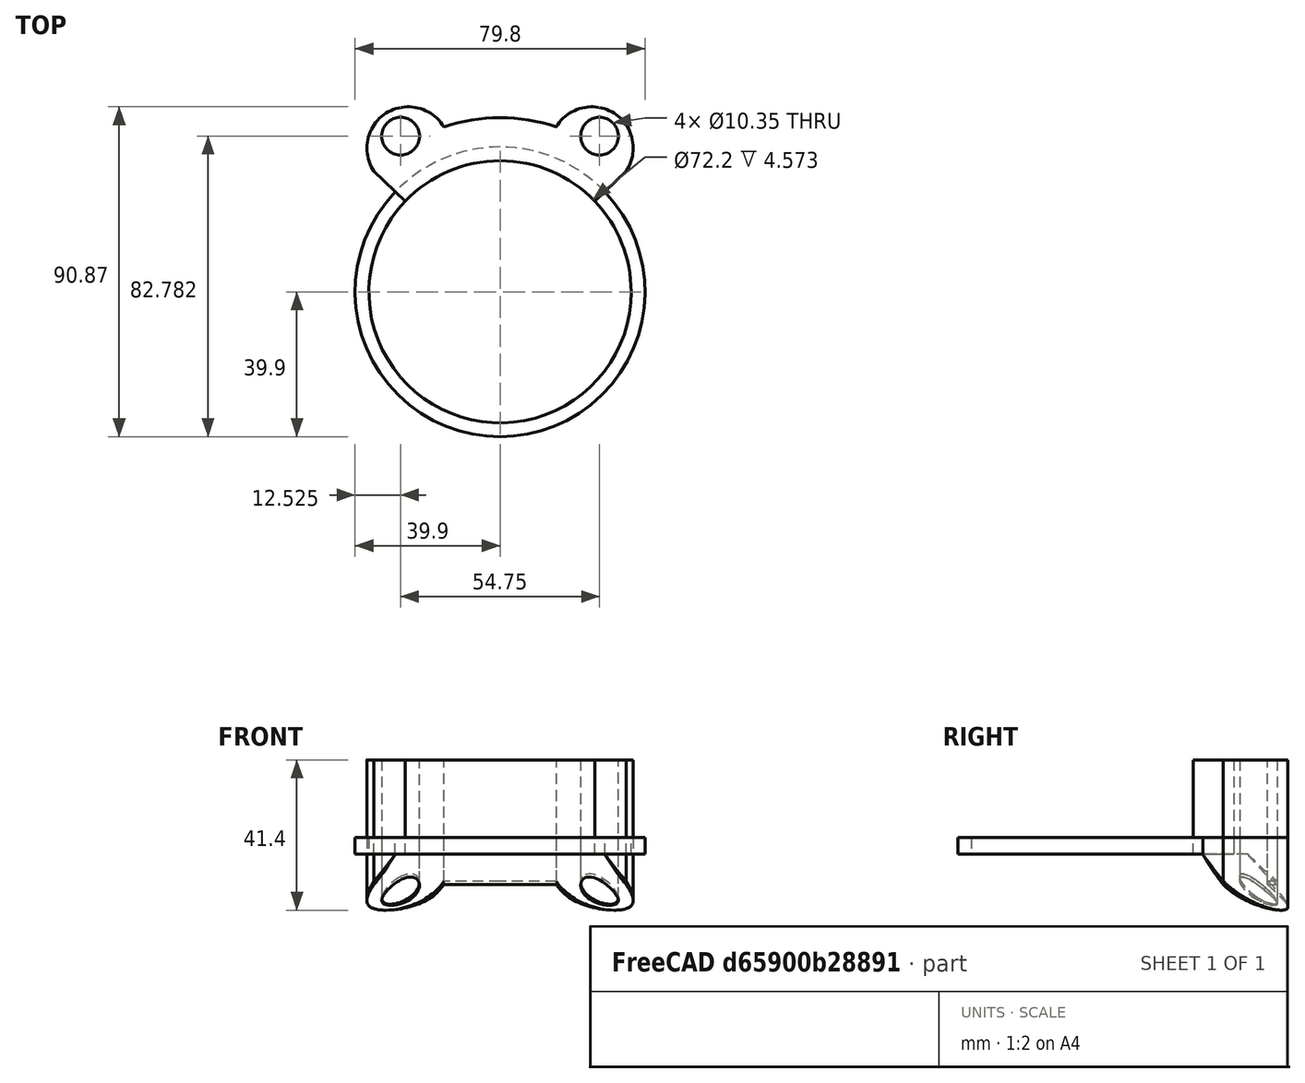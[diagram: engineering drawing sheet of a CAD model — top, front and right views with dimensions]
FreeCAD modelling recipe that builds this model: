
FCSTD DOCUMENT  (FreeCAD 0.17R13541 (Git))
Label: spacer
License: All rights reserved
LicenseURL: http://en.wikipedia.org/wiki/All_rights_reserved
objects: Mesh::Feature×11, Sketcher::SketchObject×4, PartDesign::Body×4, PartDesign::Pad×2, PartDesign::Revolution×2, Part::Cut×2, App::Part×2, App::DocumentObjectGroup×1
note: 18 computed .brp shape members not serialized (recipe doc carries the construction recipe); baked Part::Feature solids carry a one-line shape summary decoded from their .brp

FEATURE [Sketcher::SketchObject] Sketch  label="outer_sketch_right"
  MapMode = 5
  Support = -> [XY_Plane001]
  expr: Constraints.face_radius = 79.800000000000011mm / 2
  expr: Constraints[12] = 10.35mm / 2
  expr: Constraints.enclosure_radius = 96mm / 2
  expr: Constraints[27] = 22.800000000000001mm / 2
  expr: Constraints.outer_opening_outer_radius = 72.200000000000003mm / 2
  expr: Constraints.outer_opening_inner_radius = 62.799999999999997mm / 2
  sketch-geometry (34):
    g0: Circle [constr] CenterX=0 CenterY=0 CenterZ=0 NormalX=0 NormalY=0 NormalZ=1 AngleXU=0 Radius=48
    g1: Circle CenterX=-27.375 CenterY=42.8821 CenterZ=0 NormalX=0 NormalY=0 NormalZ=1 AngleXU=0 Radius=5.175
    g2: Circle [constr] CenterX=0 CenterY=0 CenterZ=0 NormalX=0 NormalY=0 NormalZ=1 AngleXU=0 Radius=36.1
    g3: Circle [constr] CenterX=0 CenterY=0 CenterZ=0 NormalX=0 NormalY=0 NormalZ=1 AngleXU=0 Radius=31.4
    g4: LineSegment [constr] StartX=0 StartY=0 StartZ=0 EndX=-31.3972 EndY=49.1827 EndZ=0
    g5: GeomPoint X=-16.8958 Y=26.4668 Z=0
    g6: GeomPoint X=-24.5904 Y=38.5201 Z=0
    g7: Circle CenterX=27.375 CenterY=42.8821 CenterZ=0 NormalX=0 NormalY=0 NormalZ=1 AngleXU=0 Radius=5.175
    g8: LineSegment [constr] StartX=0 StartY=0 StartZ=0 EndX=31.3972 EndY=49.1827 EndZ=0
    g9: GeomPoint X=16.8958 Y=26.4668 Z=0
    g10: GeomPoint X=24.5904 Y=38.5201 Z=0
    g11: LineSegment [constr] StartX=-32.55 StartY=42.8821 StartZ=0 EndX=32.55 EndY=42.8821 EndZ=0
    g12: GeomPoint X=-22.2 Y=42.8821 Z=0
    g13: GeomPoint X=22.2 Y=42.8821 Z=0
    g14: Circle [constr] CenterX=-25.263 CenterY=39.5738 CenterZ=0 NormalX=0 NormalY=0 NormalZ=1 AngleXU=0 Radius=11.4
    g15: Circle [constr] CenterX=25.263 CenterY=39.5738 CenterZ=0 NormalX=0 NormalY=0 NormalZ=1 AngleXU=0 Radius=11.4
    g16: GeomPoint X=-30.1596 Y=47.2441 Z=0
    g17: GeomPoint X=30.1596 Y=47.2441 Z=0
    g18: GeomPoint X=-34.6947 Y=33.1704 Z=0
    g19: GeomPoint X=-15.4845 Y=45.4338 Z=0
    g20: GeomPoint X=34.6947 Y=33.1704 Z=0
    g21: GeomPoint X=15.4845 Y=45.4338 Z=0
    g22: ArcOfCircle CenterX=-25.263 CenterY=39.5738 CenterZ=0 NormalX=0 NormalY=0 NormalZ=1 AngleXU=0 Radius=11.4 StartAngle=0.539887 EndAngle=3.73803
    g23: ArcOfCircle CenterX=0 CenterY=0 CenterZ=0 NormalX=0 NormalY=0 NormalZ=1 AngleXU=0 Radius=48 StartAngle=1.24233 EndAngle=1.89926
    g24: ArcOfCircle CenterX=25.263 CenterY=39.5738 CenterZ=0 NormalX=0 NormalY=0 NormalZ=1 AngleXU=0 Radius=11.4 StartAngle=5.68675 EndAngle=8.88489
    g25: LineSegment [constr] StartX=0 StartY=0 StartZ=0 EndX=-34.6947 EndY=33.1704 EndZ=0
    g26: LineSegment [constr] StartX=0 StartY=0 StartZ=0 EndX=34.6947 EndY=33.1704 EndZ=0
    g27: LineSegment StartX=-28.84 StartY=27.5729 StartZ=0 EndX=-34.6947 EndY=33.1704 EndZ=0
    g28: LineSegment StartX=28.84 StartY=27.5729 StartZ=0 EndX=34.6947 EndY=33.1704 EndZ=0
    g29: Circle [constr] CenterX=0 CenterY=0 CenterZ=0 NormalX=0 NormalY=0 NormalZ=1 AngleXU=0 Radius=39.9
    g30: GeomPoint X=-27.375 Y=42.8821 Z=0
    g31: GeomPoint X=27.375 Y=42.8821 Z=0
    g32: ArcOfCircle CenterX=0 CenterY=0 CenterZ=0 NormalX=0 NormalY=0 NormalZ=1 AngleXU=0 Radius=39.9 StartAngle=2.37865 EndAngle=7.04613
    g33: Circle CenterX=0 CenterY=0 CenterZ=0 NormalX=0 NormalY=0 NormalZ=1 AngleXU=0 Radius=36.1
  constraints (84):
    c: Coincident(g0,g-1)
    c: Radius(g0) = 48  'enclosure_radius'
    c: Coincident(g2,g-1)
    c: Radius(g2) = 36.1  'outer_opening_outer_radius'
    c: Coincident(g3,g-1)
    c: Radius(g3) = 31.4  'outer_opening_inner_radius'
    c: Coincident(g4,g-1)
    c: PointOnObject(g5,g4)
    c: PointOnObject(g5,g3)
    c: PointOnObject(g6,g4)
    c: PointOnObject(g6,g1)
    c: Distance(g5,g6) = 14.3
    c: Radius(g1) = 5.175
    c: Coincident(g8,g-1)
    c: PointOnObject(g9,g8)
    c: PointOnObject(g10,g8)
    c: PointOnObject(g9,g3)
    c: PointOnObject(g10,g7)
    c: Equal(g1,g7)
    c: Distance(g9,g10) = 14.3
    c: Horizontal(g11)
    c: PointOnObject(g12,g11)
    c: PointOnObject(g13,g11)
    c: PointOnObject(g12,g1)
    c: PointOnObject(g13,g7)
    c: PointOnObject(g14,g4)
    c: PointOnObject(g15,g8)
    c: Radius(g15) = 11.4
    c: Equal(g15,g14)
    c: PointOnObject(g1,g4)
    c: PointOnObject(g4,g14)
    c: PointOnObject(g7,g8)
    c: PointOnObject(g8,g15)
    c: PointOnObject(g16,g4)
    c: PointOnObject(g17,g8)
    c: PointOnObject(g16,g1)
    c: PointOnObject(g17,g7)
    c: Distance(g17,g8) = 2.3
    c: Distance(g16,g4) = 2.3
    c: PointOnObject(g18,g0)
    c: PointOnObject(g19,g0)
    c: PointOnObject(g20,g0)
    c: PointOnObject(g21,g0)
    c: PointOnObject(g18,g14)
    c: PointOnObject(g19,g14)
    c: PointOnObject(g21,g15)
    c: PointOnObject(g20,g15)
    c: Coincident(g22,g14)
    c: Coincident(g22,g18)
    c: PointOnObject(g22,g0)
    c: Coincident(g23,g-1)
    c: Coincident(g23,g19)
    c: PointOnObject(g23,g15)
    c: Coincident(g24,g15)
    c: Coincident(g24,g21)
    c: PointOnObject(g24,g0)
    c: Coincident(g25,g-1)
    c: Coincident(g25,g18)
    c: Coincident(g26,g-1)
    c: Coincident(g26,g20)
    c: Coincident(g27,g18)
    c: Coincident(g28,g20)
    c: Coincident(g29,g-1)
    c: Radius(g29) = 39.9  'face_radius'
    c: Distance(g-1,g4) = 58.35  'outer_radius'
    c: Distance(g5,g4) = 26.95
    c: Distance(g9,g8) = 26.95
    c: PointOnObject(g30,g11)
    c: PointOnObject(g31,g11)
    c: Coincident(g30,g1)
    c: Coincident(g31,g7)
    c: PointOnObject(g11,g1)
    c: PointOnObject(g11,g7)
    c: Distance(g11,g11) = 65.1
    c: Distance(g1,g7) = 54.75
    c: PointOnObject(g28,g29)
    c: PointOnObject(g28,g26)
    c: PointOnObject(g27,g29)
    c: PointOnObject(g27,g25)
    c: Coincident(g32,g-1)
    c: Coincident(g32,g27)
    c: PointOnObject(g32,g26)
    c: Coincident(g33,g-1)
    c: Equal(g33,g2)
FEATURE [Sketcher::SketchObject] Sketch002  label="chamfer_sketch_right"
  MapMode = 5
  Placement = pos=(0,0,0) rot=(0.57735,0.57735,0.57735;2.0944rad)
  Support = -> [YZ_Plane002]
  expr: Constraints[9] = outer_sketch.Constraints.outer_opening_outer_radius
  expr: Constraints[8] = Sketch.Constraints.outer_radius
  expr: Constraints[10] = Sketch.Constraints.face_radius
  sketch-geometry (7):
    g0: LineSegment StartX=36.1 StartY=15.4272 StartZ=0 EndX=39.9 EndY=15.4272 EndZ=0
    g1: LineSegment [constr] StartX=39.9 StartY=15.4272 StartZ=0 EndX=58.35 EndY=1.2e-11 EndZ=0
    g2: LineSegment StartX=58.35 StartY=1.2e-11 StartZ=0 EndX=58.35 EndY=-5 EndZ=0
    g3: LineSegment StartX=58.35 StartY=-5 StartZ=0 EndX=36.1 EndY=-5 EndZ=0
    g4: LineSegment StartX=36.1 StartY=-5 StartZ=0 EndX=36.1 EndY=15.4272 EndZ=0
    g5: LineSegment [constr] StartX=49.125 StartY=7.71362 StartZ=0 EndX=48.8043 EndY=7.33005 EndZ=0
    g6: ArcOfCircle CenterX=141.721 CenterY=118.452 CenterZ=0 NormalX=0 NormalY=0 NormalZ=1 AngleXU=0 Radius=144.851 StartAngle=3.93287 EndAngle=4.09909
  constraints (22):
    c: Horizontal(g0)
    c: Coincident(g0,g1)
    c: Vertical(g2)
    c: Coincident(g2,g3)
    c: Horizontal(g3)
    c: Coincident(g3,g4)
    c: Coincident(g4,g0)
    c: Vertical(g4)
    c: DistanceX(g-1,g1) = 58.35
    c: DistanceX(g-1,g0) = 36.1
    c: DistanceX(g-1,g0) = 39.9
    c: Coincident(g1,g2)
    c: PointOnObject(g1,g-1)
    c: Distance(g2) = 5
    c: Distance(g1) = 24.05
    c: PointOnObject(g5,g1)
    c: Perpendicular(g1,g5)
    c: Symmetric(g0,g1,g5)
    c: Distance(g5) = 0.5  'chamfer_deflection'
    c: Coincident(g6,g0)
    c: Coincident(g6,g1)
    c: PointOnObject(g5,g6)
FEATURE [PartDesign::Pad] Pad
  Length = 20
  Length2 = 100
  Profile = -> Sketch
  Type = 0
FEATURE [PartDesign::Body] Body  label="case_right"
  Group = -> [Sketch,Pad]
  Origin = -> Origin001
  Tip = -> Pad
FEATURE [PartDesign::Revolution] Revolution
  Angle = 360
  Axis = (0,0,1)
  Base = (0,0,0)
  Placement = pos=(0,0,0) rot=(0.57735,0.57735,0.57735;2.0944rad)
  Profile = -> Sketch002
  ReferenceAxis = -> Sketch002 [V_Axis]
  Reversed = true
FEATURE [PartDesign::Body] Body001  label="chamfer_cutout_right"
  Group = -> [Sketch002,Revolution]
  Origin = -> Origin002
  Tip = -> Revolution
FEATURE [Mesh::Feature] Mesh  label="spacer_mesh"
FEATURE [Mesh::Feature] Mesh001  label="spacer_mesh2-0"
FEATURE [Mesh::Feature] Mesh002  label="spacer_mesh2-1.2"
FEATURE [Mesh::Feature] Mesh003  label="spacer_mesh3-1.2"
FEATURE [Mesh::Feature] Mesh004  label="spacer_mesh3-0.5"
FEATURE [Mesh::Feature] Mesh005  label="spacer_mesh4-0.5"
FEATURE [Mesh::Feature] Mesh006  label="spacer_mesh4-1.2"
FEATURE [Mesh::Feature] Mesh007  label="spacer_mesh5-1.2"
FEATURE [Mesh::Feature] Mesh008  label="spacer_mesh5-0.5"
FEATURE [Sketcher::SketchObject] Sketch004  label="outer_sketch001"
  MapMode = 5
  Support = -> [XY_Plane005]
  expr: Constraints.outer_opening_inner_radius = 62.799999999999997mm / 2
  expr: Constraints.outer_opening_outer_radius = 72.200000000000003mm / 2
  expr: Constraints[27] = 22.800000000000001mm / 2
  expr: Constraints.enclosure_radius = 96mm / 2
  expr: Constraints.face_radius = 79.800000000000011mm / 2
  expr: Constraints[12] = 10.35mm / 2
  sketch-geometry (33):
    g0: Circle [constr] CenterX=0 CenterY=0 CenterZ=0 NormalX=0 NormalY=0 NormalZ=1 AngleXU=0 Radius=48
    g1: Circle CenterX=-27.375 CenterY=42.8821 CenterZ=0 NormalX=0 NormalY=0 NormalZ=1 AngleXU=0 Radius=5.175
    g2: Circle [constr] CenterX=0 CenterY=0 CenterZ=0 NormalX=0 NormalY=0 NormalZ=1 AngleXU=0 Radius=36.1
    g3: Circle [constr] CenterX=0 CenterY=0 CenterZ=0 NormalX=0 NormalY=0 NormalZ=1 AngleXU=0 Radius=31.4
    g4: LineSegment [constr] StartX=0 StartY=0 StartZ=0 EndX=-31.3972 EndY=49.1827 EndZ=0
    g5: GeomPoint X=-16.8958 Y=26.4668 Z=0
    g6: GeomPoint X=-24.5904 Y=38.5201 Z=0
    g7: Circle CenterX=27.375 CenterY=42.8821 CenterZ=0 NormalX=0 NormalY=0 NormalZ=1 AngleXU=0 Radius=5.175
    g8: LineSegment [constr] StartX=0 StartY=0 StartZ=0 EndX=31.3972 EndY=49.1827 EndZ=0
    g9: GeomPoint X=16.8958 Y=26.4668 Z=0
    g10: GeomPoint X=24.5904 Y=38.5201 Z=0
    g11: LineSegment [constr] StartX=-32.55 StartY=42.8821 StartZ=0 EndX=32.55 EndY=42.8821 EndZ=0
    g12: GeomPoint X=-22.2 Y=42.8821 Z=0
    g13: GeomPoint X=22.2 Y=42.8821 Z=0
    g14: Circle [constr] CenterX=-25.263 CenterY=39.5738 CenterZ=0 NormalX=0 NormalY=0 NormalZ=1 AngleXU=0 Radius=11.4
    g15: Circle [constr] CenterX=25.263 CenterY=39.5738 CenterZ=0 NormalX=0 NormalY=0 NormalZ=1 AngleXU=0 Radius=11.4
    g16: GeomPoint X=-30.1596 Y=47.2441 Z=0
    g17: GeomPoint X=30.1596 Y=47.2441 Z=0
    g18: GeomPoint X=-34.6947 Y=33.1704 Z=0
    g19: GeomPoint X=-15.4845 Y=45.4338 Z=0
    g20: GeomPoint X=34.6947 Y=33.1704 Z=0
    g21: GeomPoint X=15.4845 Y=45.4338 Z=0
    g22: ArcOfCircle CenterX=-25.263 CenterY=39.5738 CenterZ=0 NormalX=0 NormalY=0 NormalZ=1 AngleXU=0 Radius=11.4 StartAngle=0.539887 EndAngle=3.73803
    g23: ArcOfCircle CenterX=0 CenterY=0 CenterZ=0 NormalX=0 NormalY=0 NormalZ=1 AngleXU=0 Radius=48 StartAngle=1.24233 EndAngle=1.89926
    g24: ArcOfCircle CenterX=25.263 CenterY=39.5738 CenterZ=0 NormalX=0 NormalY=0 NormalZ=1 AngleXU=0 Radius=11.4 StartAngle=5.68675 EndAngle=8.88489
    g25: LineSegment [constr] StartX=0 StartY=0 StartZ=0 EndX=-34.6947 EndY=33.1704 EndZ=0
    g26: LineSegment [constr] StartX=0 StartY=0 StartZ=0 EndX=34.6947 EndY=33.1704 EndZ=0
    g27: ArcOfCircle CenterX=0 CenterY=0 CenterZ=0 NormalX=0 NormalY=0 NormalZ=1 AngleXU=0 Radius=36.1 StartAngle=0.762941 EndAngle=2.37865
    g28: LineSegment StartX=-26.0933 StartY=24.9469 StartZ=0 EndX=-34.6947 EndY=33.1704 EndZ=0
    g29: LineSegment StartX=26.0933 StartY=24.9469 StartZ=0 EndX=34.6947 EndY=33.1704 EndZ=0
    g30: Circle [constr] CenterX=0 CenterY=0 CenterZ=0 NormalX=0 NormalY=0 NormalZ=1 AngleXU=0 Radius=39.9
    g31: GeomPoint X=-27.375 Y=42.8821 Z=0
    g32: GeomPoint X=27.375 Y=42.8821 Z=0
  constraints (81):
    c: Coincident(g0,g-1)
    c: Radius(g0) = 48  'enclosure_radius'
    c: Coincident(g2,g-1)
    c: Radius(g2) = 36.1  'outer_opening_outer_radius'
    c: Coincident(g3,g-1)
    c: Radius(g3) = 31.4  'outer_opening_inner_radius'
    c: Coincident(g4,g-1)
    c: PointOnObject(g5,g4)
    c: PointOnObject(g5,g3)
    c: PointOnObject(g6,g4)
    c: PointOnObject(g6,g1)
    c: Distance(g5,g6) = 14.3
    c: Radius(g1) = 5.175
    c: Coincident(g8,g-1)
    c: PointOnObject(g9,g8)
    c: PointOnObject(g10,g8)
    c: PointOnObject(g9,g3)
    c: PointOnObject(g10,g7)
    c: Equal(g1,g7)
    c: Distance(g9,g10) = 14.3
    c: Horizontal(g11)
    c: PointOnObject(g12,g11)
    c: PointOnObject(g13,g11)
    c: PointOnObject(g12,g1)
    c: PointOnObject(g13,g7)
    c: PointOnObject(g14,g4)
    c: PointOnObject(g15,g8)
    c: Radius(g15) = 11.4
    c: Equal(g15,g14)
    c: PointOnObject(g1,g4)
    c: PointOnObject(g4,g14)
    c: PointOnObject(g7,g8)
    c: PointOnObject(g8,g15)
    c: PointOnObject(g16,g4)
    c: PointOnObject(g17,g8)
    c: PointOnObject(g16,g1)
    c: PointOnObject(g17,g7)
    c: Distance(g17,g8) = 2.3
    c: Distance(g16,g4) = 2.3
    c: PointOnObject(g18,g0)
    c: PointOnObject(g19,g0)
    c: PointOnObject(g20,g0)
    c: PointOnObject(g21,g0)
    c: PointOnObject(g18,g14)
    c: PointOnObject(g19,g14)
    c: PointOnObject(g21,g15)
    c: PointOnObject(g20,g15)
    c: Coincident(g22,g14)
    c: Coincident(g22,g18)
    c: PointOnObject(g22,g0)
    c: Coincident(g23,g-1)
    c: Coincident(g23,g19)
    c: PointOnObject(g23,g15)
    c: Coincident(g24,g15)
    c: Coincident(g24,g21)
    c: PointOnObject(g24,g0)
    c: Coincident(g25,g-1)
    c: Coincident(g25,g18)
    c: Coincident(g26,g-1)
    c: Coincident(g26,g20)
    c: Coincident(g27,g-1)
    c: PointOnObject(g27,g2)
    c: PointOnObject(g27,g26)
    c: PointOnObject(g27,g25)
    c: Coincident(g28,g27)
    c: Coincident(g28,g18)
    c: Coincident(g29,g27)
    c: Coincident(g29,g20)
    c: Coincident(g30,g-1)
    c: Radius(g30) = 39.9  'face_radius'
    c: Distance(g-1,g4) = 58.35  'outer_radius'
    c: Distance(g5,g4) = 26.95
    c: Distance(g9,g8) = 26.95
    c: PointOnObject(g31,g11)
    c: PointOnObject(g32,g11)
    c: Coincident(g31,g1)
    c: Coincident(g32,g7)
    c: PointOnObject(g11,g1)
    c: PointOnObject(g11,g7)
    c: Distance(g11,g11) = 65.1
    c: Distance(g1,g7) = 54.75
FEATURE [Sketcher::SketchObject] Sketch005  label="chamfer_sketch_left"
  MapMode = 5
  Placement = pos=(0,0,0) rot=(0.57735,0.57735,0.57735;2.0944rad)
  Support = -> [YZ_Plane006]
  expr: Constraints[9] = outer_sketch.Constraints.outer_opening_outer_radius
  expr: Constraints[8] = Sketch.Constraints.outer_radius
  expr: Constraints[10] = Sketch.Constraints.face_radius
  sketch-geometry (7):
    g0: LineSegment StartX=36.1 StartY=15.4272 StartZ=0 EndX=39.9 EndY=15.4272 EndZ=0
    g1: LineSegment [constr] StartX=39.9 StartY=15.4272 StartZ=0 EndX=58.35 EndY=0 EndZ=0
    g2: LineSegment StartX=58.35 StartY=0 StartZ=0 EndX=58.35 EndY=-5 EndZ=0
    g3: LineSegment StartX=58.35 StartY=-5 StartZ=0 EndX=36.1 EndY=-5 EndZ=0
    g4: LineSegment StartX=36.1 StartY=-5 StartZ=0 EndX=36.1 EndY=15.4272 EndZ=0
    g5: LineSegment [constr] StartX=49.125 StartY=7.71362 StartZ=0 EndX=48.3552 EndY=6.79304 EndZ=0
    g6: ArcOfCircle CenterX=87.3886 CenterY=53.4744 CenterZ=0 NormalX=0 NormalY=0 NormalZ=1 AngleXU=0 Radius=60.8503 StartAngle=3.81706 EndAngle=4.21491
  constraints (22):
    c: Horizontal(g0)
    c: Coincident(g0,g1)
    c: Vertical(g2)
    c: Coincident(g2,g3)
    c: Horizontal(g3)
    c: Coincident(g3,g4)
    c: Coincident(g4,g0)
    c: Vertical(g4)
    c: DistanceX(g-1,g1) = 58.35
    c: DistanceX(g-1,g0) = 36.1
    c: DistanceX(g-1,g0) = 39.9
    c: Coincident(g1,g2)
    c: PointOnObject(g1,g-1)
    c: Distance(g2) = 5
    c: Distance(g1) = 24.05
    c: PointOnObject(g5,g1)
    c: Perpendicular(g1,g5)
    c: Symmetric(g0,g1,g5)
    c: Distance(g5) = 1.2  'chamfer_deflection'
    c: Coincident(g6,g0)
    c: Coincident(g6,g1)
    c: PointOnObject(g5,g6)
FEATURE [PartDesign::Pad] Pad002
  Length = 41.4
  Length2 = 100
  Profile = -> Sketch004
  Type = 0
FEATURE [PartDesign::Body] Body005  label="case_left"
  Group = -> [Sketch004,Pad002]
  Origin = -> Origin006
  Tip = -> Pad002
FEATURE [PartDesign::Revolution] Revolution001
  Angle = 360
  Axis = (0,0,1)
  Base = (0,0,0)
  Placement = pos=(0,0,0) rot=(0.57735,0.57735,0.57735;2.0944rad)
  Profile = -> Sketch005
  ReferenceAxis = -> Sketch005 [V_Axis]
  Reversed = true
FEATURE [PartDesign::Body] Body004  label="chamfer_cutout_left"
  Group = -> [Sketch005,Revolution001]
  Origin = -> Origin007
  Tip = -> Revolution001
FEATURE [Part::Cut] Cut  label="spacer_right"
  Base = -> Body
  Tool = -> Body001
FEATURE [App::Part] Part  label="spacer_right_part"
  Group = -> [Body,Body001,Cut]
  License = CC BY 3.0
  LicenseURL = http://creativecommons.org/licenses/by/3.0/
  Origin = -> Origin
FEATURE [Part::Cut] Cut001  label="spacer_left"
  Base = -> Body005
  Tool = -> Body004
FEATURE [App::Part] Part001  label="spacer_left_part"
  Group = -> [Body005,Body004,Cut001]
  License = CC BY 3.0
  LicenseURL = http://creativecommons.org/licenses/by/3.0/
  Origin = -> Origin005
FEATURE [Mesh::Feature] Mesh009  label="spacer_left_mesh6"
FEATURE [Mesh::Feature] Mesh010  label="spacer_right_mesh6"
FEATURE [App::DocumentObjectGroup] Group  label="mesh"
  Group = -> [Mesh,Mesh001,Mesh002,Mesh003,Mesh004,Mesh005,Mesh006,Mesh007,Mesh008,Mesh009,Mesh010]
